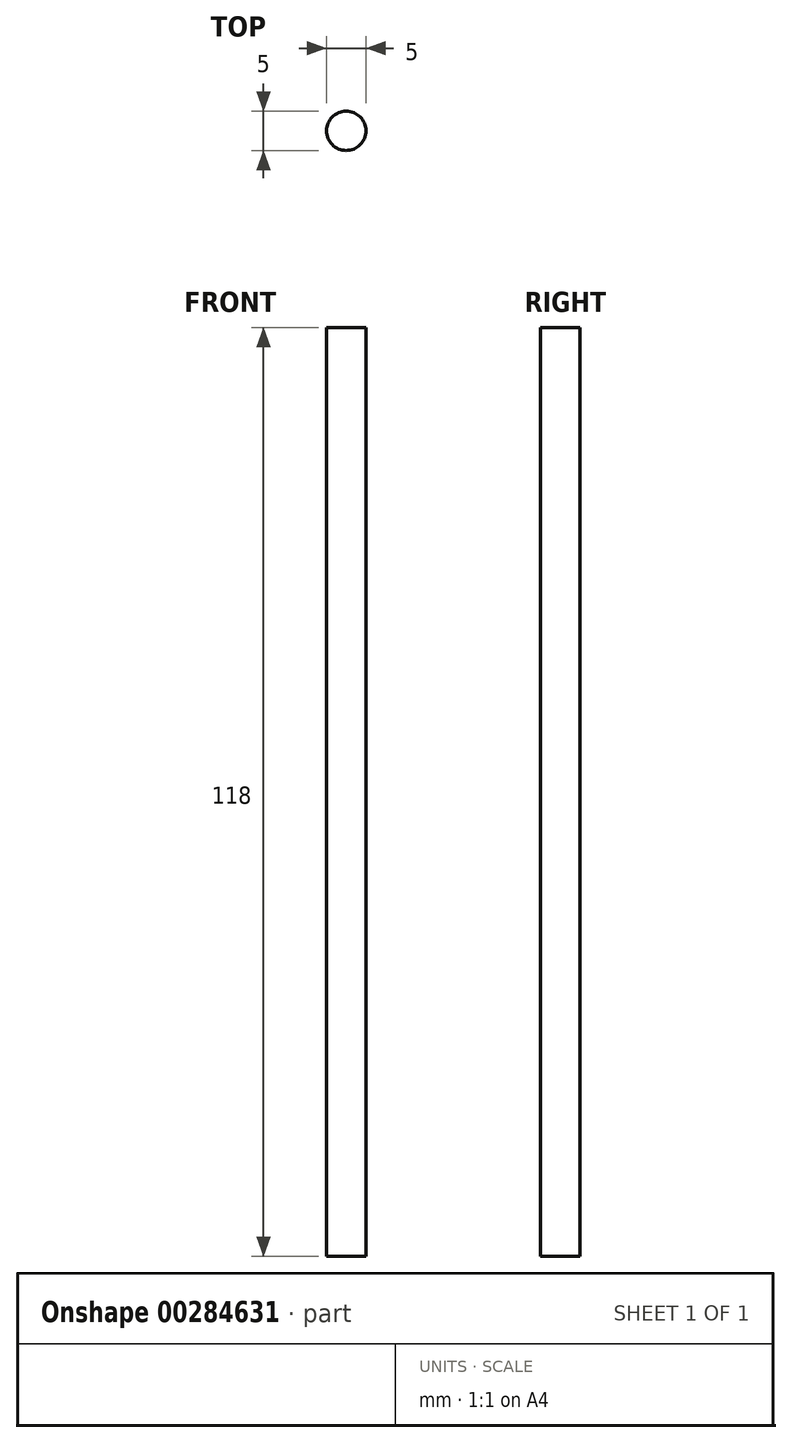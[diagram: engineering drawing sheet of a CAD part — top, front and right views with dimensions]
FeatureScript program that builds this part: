
annotation { "Feature Type Name" : "Feature", "Feature Type Description" : "" }
export const myFeature = defineFeature(function(context is Context, id is Id, definition is map)
    precondition{}
    {
        {
            var Q0;
            Q0=qCreatedBy(makeId("Top.planeOp"),FACE);
            var sketch = newSketch(context, id + "F0", { "sketchPlane" : qUnion([Q0])});
            skCircle(sketch, "E0", {"center": v(0, 0) * mm, "radius": 2.5 * mm});
            skSolve(sketch);
        }
        {
            var Q0;
            Q0 = qSketchRegion(id + "F0", true);
            extrude(context, id + "F1", {"entities" : qUnion([Q0]), "endBound" : BoundingType.SYMMETRIC, "depth" : 118 * mm});
        }
    });
